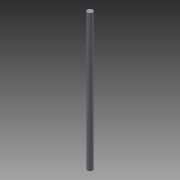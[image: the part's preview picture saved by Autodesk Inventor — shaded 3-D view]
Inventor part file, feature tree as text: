
AUTODESK INVENTOR PART (.ipt)
format: ipt  version: 2015 SP1 (Build 190203100, 203)  size: 64,512 bytes
history: native  units: mm
features: extrude x1, sketch x1
ambient origin geometry x8: Origin, YZ Plane, XZ Plane, XY Plane, X Axis, Y Axis, Z Axis, Center Point
bodies: Solid1 (feature_tree)
feature tree (2):
  extrude  "Extrusion1"  Depth=103.6mm TaperAngle=0.0deg
  sketch  "Sketch1"  dims[d0=4.0mm d1=103.6mm d2=0.0mm]
